# Revit family: M_Podwójne - szkło 2
name_source: partatom
category: Doors
revit_build: Autodesk Revit 2014 (Build: 20130126_1515(x64)
units: mm (PartAtom-declared; Revit-internal decimal feet)

## types (5) — shared parameters
Function = Interior
Materiał drzwi = Drzwi - panel
Materiał ramy = Drzwi - rama
Rzut przycięcia - wewnętrzny = 25 mm  [stored 0.082021 ft]
Rzut przycięcia - zewnętrzny = 25 mm  [stored 0.082021 ft]
Szpros = 25 mm  [stored 0.082021 ft]
Thickness = 51 mm  [stored 0.167323 ft]
Wall Closure = By host

## per-type parameters (varying)
| type | Analytic Construction | Construction Type Id | Heat Transfer Coefficient (U) | Height | Solar Heat Gain Coefficient | Szerokość przycięcia | Thermal Resistance (R) | Visual Light Transmittance | Width |
| 1830 x 1981 mm | 1/8 cala pojedyncze przeszklenie Pilkington | GSP4R | 3.6886 W/(m²·K) | 1981 mm | 0.78 | 76 mm | 0.0000 (m²·K)/W | 0.9 | 1830 mm  [stored 6.00394 ft] |
| 1830 x 2083 mm | 1/8 cala pojedyncze przeszklenie Pilkington | GSP4R | 3.6886 W/(m²·K) | 2083 mm  [stored 6.83399 ft] | 0.78 | 76 mm | 0.0000 (m²·K)/W | 0.9 | 1830 mm  [stored 6.00394 ft] |
| 1730 x 2032 mm | 1/8 cala pojedyncze przeszklenie Pilkington | GSP4R | 3.6886 W/(m²·K) | 2032 mm  [stored 6.66667 ft] | 0.78 | 76 mm | 0.0000 (m²·K)/W | 0.9 | 1730 mm |
| 1730 x 2134 mm | 1/8 cala pojedyncze przeszklenie Pilkington | GSP4R | 3.6886 W/(m²·K) | 2134 mm  [stored 7.00131 ft] | 0.78 | 76 mm | 0.0000 (m²·K)/W | 0.9 | 1730 mm |
| 1830 x 2134 mm | Metal | MDRZWI | 3.7021 W/(m²·K) | 2134 mm  [stored 7.00131 ft] | 0 | 76.2 mm  [stored 0.25 ft] | 0.2701 (m²·K)/W | 0 | 1830 mm  [stored 6.00394 ft] |

note: [stored X ft] marks values corroborated as IEEE doubles in the binary element streams (Revit-internal decimal feet)
